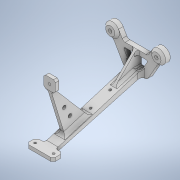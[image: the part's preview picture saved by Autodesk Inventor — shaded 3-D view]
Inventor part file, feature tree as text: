
AUTODESK INVENTOR PART (.ipt)
format: ipt  version: 2023 (Build 270158000, 158)  size: 513,024 bytes
history: native  units: mm
features: extrude x16, sketch x15, projected_geometry x15, fillet x13, reference x6, other x6, plane x3, chamfer x3, thicken_offset x2, mirror x1
ambient origin geometry x8: Origin, YZ Plane, XZ Plane, XY Plane, X Axis, Y Axis, Z Axis, Center Point
bodies: Solid1 (feature_tree)
feature tree (80):
  extrude  "Extrusion1"  Depth=12.0mm
  extrude  "Extrusion2"  Depth=4.0mm
  plane  "Work Plane1"
  extrude  "Extrusion3"  Depth=5.0mm
  extrude  "Extrusion4"  Depth=5.0mm
  sketch  "Sketch5"  dims[d7=10.0mm d8=0.0mm d9=5.0mm]
  plane  "Work Plane2"
  extrude  "Extrusion5"  Depth=2.0mm
  extrude  "Extrusion6"  Depth=4.0mm
  mirror  "Mirror1"
  extrude  "Extrusion7"  Depth=10.0mm TaperAngle=0.0deg
  extrude  "Extrusion8"  Depth=23.0mm
  extrude  "Extrusion9"  Depth=2.0mm
  plane  "Work Plane3"
  extrude  "Extrusion10"  Depth=3.0mm TaperAngle=0.0deg
  extrude  "Extrusion11"  Depth=6.0mm TaperAngle=0.0deg
  fillet  "Fillet1"  Radius=4.0mm
  fillet  "Fillet2"  Radius=4.0mm
  fillet  "Fillet3"  Radius=6.0mm
  chamfer  "Chamfer2"  Distance=2.0mm
  chamfer  "Chamfer3"  Distance=2.0mm
  fillet  "Fillet4"  Radius=5.0mm
  extrude  "Extrusion12"  Depth=3.0mm
  thicken_offset  "Thicken1"
  thicken_offset  "Thicken2"
  fillet  "Fillet5"  Radius=10.0mm
  fillet  "Fillet6"  Radius=10.0mm
  fillet  "Fillet7"  Radius=20.0mm
  fillet  "Fillet8"  Radius=3.0mm
  fillet  "Fillet9"  Radius=2.0mm
  fillet  "Fillet10"  Radius=3.0mm
  fillet  "Fillet11"  Radius=3.0mm
  fillet  "Fillet12"  Radius=2.0mm
  fillet  "Fillet13"  Radius=2.0mm
  extrude  "Extrusion13"  Depth=2.0mm
  extrude  "Extrusion14"  Depth=10.0mm
  extrude  "Extrusion15"  Depth=2.0mm
  extrude  "Extrusion16"  Depth=3.0mm TaperAngle=0.0deg
  chamfer  "Chamfer4"  Distance=2.0mm
  reference  "Reference1"
  reference  "Reference2"
  sketch  "Sketch2"  dims[d0=12.0mm d1=12.0mm]
  projected_geometry  "Projected Loop1"
  projected_geometry  "Projected Loop2"
  sketch  "Sketch3"  dims[d2=4.0mm d3=0.0mm d4=20.0mm]
  reference  "Reference3"
  sketch  "Sketch4"  dims[d5=5.0mm d6=20.0mm]
  reference  "Reference4"
  projected_geometry  "Projected Loop3"
  projected_geometry  "Projected Loop4"
  projected_geometry  "Projected Loop5"
  sketch  "Sketch6"  dims[d10=2.0mm d11=7.0mm]
  projected_geometry  "Projected Loop6"
  sketch  "Sketch7"  dims[d12=4.0mm d13=11.0mm]
  projected_geometry  "Projected Loop7"
  sketch  "Sketch8"  dims[d14=3.0mm d15=10.0mm d16=0.0mm]
  projected_geometry  "Projected Loop8"
  projected_geometry  "Projected Loop9"
  sketch  "Sketch9"  dims[d17=8.0mm d18=23.0mm]
  projected_geometry  "Projected Loop10"
  sketch  "Sketch10"  dims[d19=2.0mm d20=2.0mm]
  reference  "Reference5"
  sketch  "Sketch11"  dims[d21=3.0mm d22=0.0mm d23=3.0mm d24=0.0mm]
  projected_geometry  "Projected Loop11"
  projected_geometry  "Projected Loop12"
  sketch  "Sketch12"  dims[d25=12.0mm d26=6.0mm d27=0.0mm d28=4.0mm d29=4.0mm d30=6.0mm d31=0.0mm]
  projected_geometry  "Projected Loop13"
  sketch  "Sketch13"  dims[d32=13.5mm]
  reference  "Reference6"
  sketch  "Sketch14"  dims[d33=20.0mm d34=2.0mm d35=0.0mm d36=2.0mm d37=0.0mm d38=5.0mm]
  projected_geometry  "Projected Loop14"
  sketch  "Sketch15"  dims[d39=5.0mm d40=3.0mm d41=10.0mm d42=10.0mm d43=0.0mm d44=20.0mm d45=3.0mm d46=0.0mm d47=2.0mm d48=3.0mm d49=3.0mm]
  projected_geometry  "Projected Loop15"
  sketch  "Sketch16"  dims[d53=1.5mm d54=2.0mm d55=45.0deg d56=2.0mm d57=2.0mm d58=45.0deg d59=2.0mm d60=3.1mm d61=10.0mm d62=3.1mm d63=3.0mm d64=0.0mm d65=2.0mm d66=2.0mm d67=2.0mm d68=2.0mm d69=3.0mm d70=3.0mm d71=3.0mm d72=1.0mm d73=3.0mm d74=1.0mm d75=2.0mm d76=3.0mm d77=3.0mm d78=2.0mm d79=3.0mm d80=0.0mm d81=3.0mm d82=3.0mm d83=2.0mm d84=2.0mm d85=6.0mm d86=0.0mm d87=8.0mm d88=8.0mm d89=2.0mm d90=0.0mm d91=3.0mm d92=3.0mm d93=8.0mm d94=0.0mm d95=2.0mm d96=2.0mm d97=45.0deg]
  parser-record x1  (decoder bookkeeping rows leaked as tree rows — omitted from the tree; the rows remain in map.json)
  other  "body_1.iam"
  other  "body_conn_2:1"
  other  "body_conn_2_MIR:1"
  other  "body_shell_1:1"
  other  "body_shell_2:1"
note: 1 file-system path scrubbed to <path> (originals preserved in map.json)
